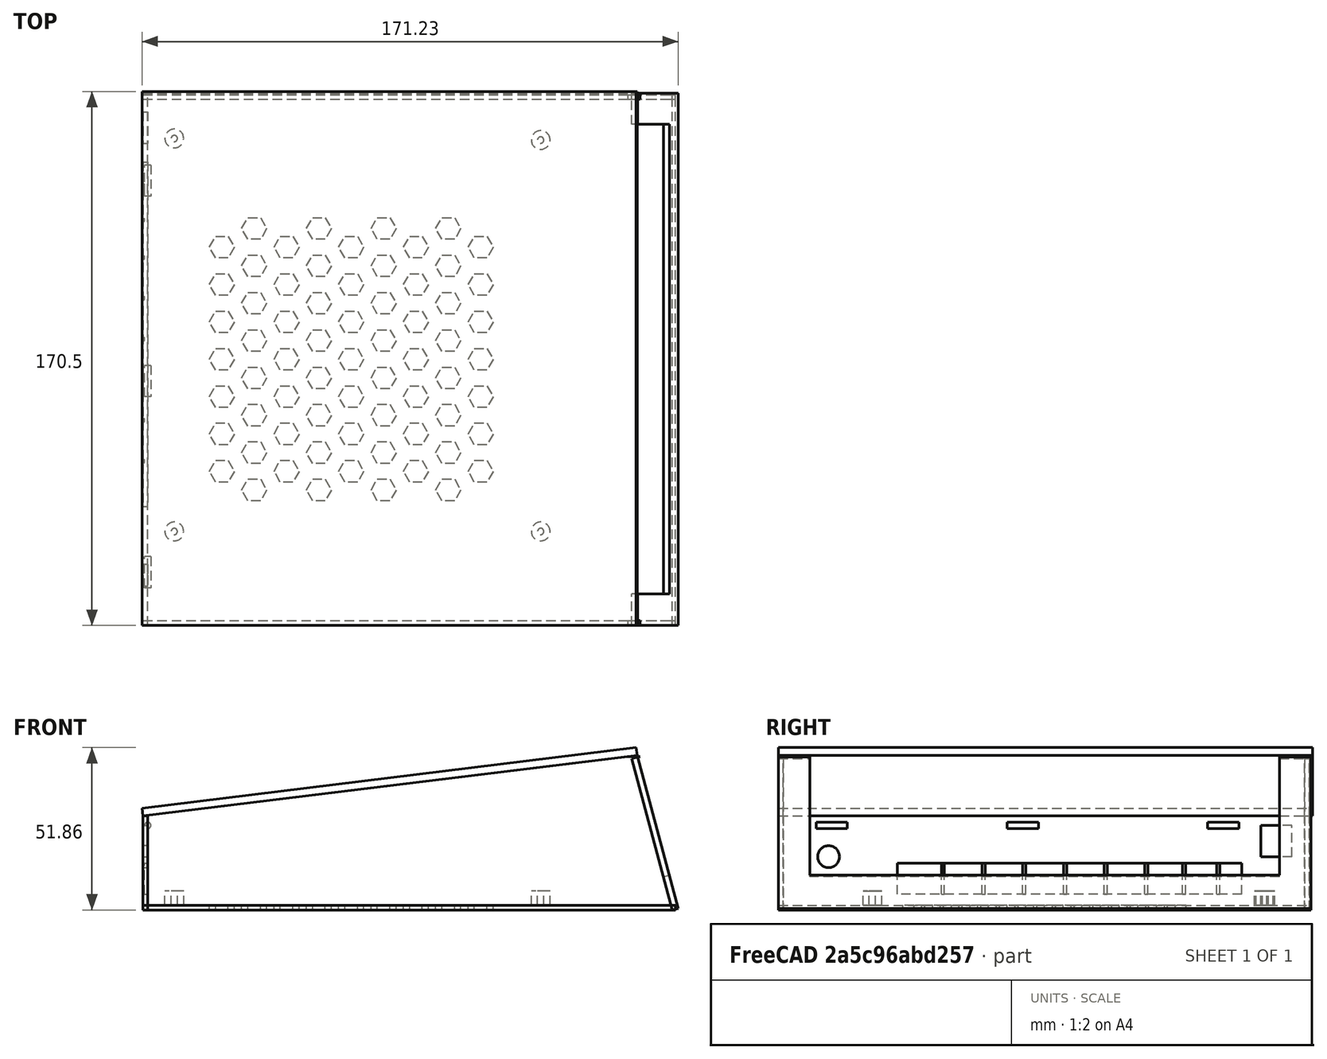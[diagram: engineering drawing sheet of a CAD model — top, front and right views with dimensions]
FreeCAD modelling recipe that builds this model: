
FCSTD DOCUMENT  (FreeCAD 0.20R29603 (Git))
Label: case3
License: All rights reserved
LicenseURL: http://en.wikipedia.org/wiki/All_rights_reserved
objects: Part::Box×21, Part::Cut×9, Part::FeaturePython×5, Part::Cylinder×4, Part::MultiFuse×2, App::DocumentObjectGroup×2
note: 41 computed .brp shape members not serialized (recipe doc carries the construction recipe); baked Part::Feature solids carry a one-line shape summary decoded from their .brp

FEATURE [Part::Box] Box  label="base"
  AttacherType = Attacher::AttachEngine3D
  Height = 1.5
  Length = 170
  Placement = pos=(0,0,-10) rot=(1,0,0;0rad)
  Width = 170
FEATURE [Part::Box] Box001  label="Face"
  AttacherType = Attacher::AttachEngine3D
  Height = 50
  Length = 2
  Placement = pos=(169,0,-10) rot=(0,-1,0;0.261799rad)
  Width = 170
FEATURE [Part::Box] Box002  label="Cube002"
  AttacherType = Attacher::AttachEngine3D
  Height = 30
  Length = 1.5
  Placement = pos=(0,0,-10) rot=(0,0,1;0rad)
  Width = 170
FEATURE [Part::FeaturePython] Tube002  # WARN: FeaturePython — macro-defined, semantics opaque (R4)
  AttacherType = Attacher::AttachEngine3D
  Height = 5
  InnerRadius = 1
  OuterRadius = 3
  Placement = pos=(10,10,-9) rot=(0,0,1;0rad)
FEATURE [Part::FeaturePython] Tube003  # WARN: FeaturePython — macro-defined, semantics opaque (R4)
  AttacherType = Attacher::AttachEngine3D
  Height = 5
  InnerRadius = 1
  OuterRadius = 3
  Placement = pos=(10,135.5,-9) rot=(0,0,1;0rad)
FEATURE [Part::FeaturePython] Tube004  # WARN: FeaturePython — macro-defined, semantics opaque (R4)
  AttacherType = Attacher::AttachEngine3D
  Height = 5
  InnerRadius = 1
  OuterRadius = 3
  Placement = pos=(127,135,-9) rot=(0,0,1;0rad)
FEATURE [Part::FeaturePython] Tube005  # WARN: FeaturePython — macro-defined, semantics opaque (R4)
  AttacherType = Attacher::AttachEngine3D
  Height = 5
  InnerRadius = 1
  OuterRadius = 3
  Placement = pos=(127,10,-9) rot=(0,0,1;0rad)
FEATURE [Part::Box] Box004  label="Cube003"
  AttacherType = Attacher::AttachEngine3D
  Height = 10
  Length = 10
  Placement = pos=(-3,38,-5) rot=(0,0,1;0rad)
  Width = 110
FEATURE [Part::MultiFuse] Fusion003
  Placement = pos=(0,20,0) rot=(0,0,1;0rad)
  Shapes = -> [Tube002,Tube003,Tube004,Tube005]
FEATURE [Part::Cylinder] Cylinder004  label="pwrjack"
  Angle = 360
  AttacherType = Attacher::AttachEngine3D
  FirstAngle = 0
  Height = 10
  Placement = pos=(-3,16,7) rot=(0,1,0;1.5708rad)
  Radius = 3.5
  SecondAngle = 0
FEATURE [Part::Cut] Cut003
  Base = -> Box002
  Tool = -> Cylinder004
FEATURE [Part::Box] Box012  label="Cube010"
  AttacherType = Attacher::AttachEngine3D
  Height = 10
  Length = 0.5
  Placement = pos=(0,65,-5) rot=(0,0,1;0rad)
  Width = 1
FEATURE [Part::Box] Box013  label="Cube011"
  AttacherType = Attacher::AttachEngine3D
  Height = 10
  Length = 0.5
  Placement = pos=(0,52,-5) rot=(0,0,1;0rad)
  Width = 1
FEATURE [Part::Box] Box014  label="Cube012"
  AttacherType = Attacher::AttachEngine3D
  Height = 10
  Length = 0.5
  Placement = pos=(0,78,-5) rot=(0,0,1;0rad)
  Width = 1
FEATURE [Part::Box] Box015  label="Cube013"
  AttacherType = Attacher::AttachEngine3D
  Height = 10
  Length = 0.5
  Placement = pos=(0,91,-5) rot=(0,0,1;0rad)
  Width = 1
FEATURE [Part::Box] Box016  label="Cube014"
  AttacherType = Attacher::AttachEngine3D
  Height = 10
  Length = 0.5
  Placement = pos=(0,104,-5) rot=(0,0,1;0rad)
  Width = 1
FEATURE [Part::Box] Box017  label="Cube015"
  AttacherType = Attacher::AttachEngine3D
  Height = 10
  Length = 0.5
  Placement = pos=(0,117,-5) rot=(0,0,1;0rad)
  Width = 1
FEATURE [Part::Box] Box018  label="Cube016"
  AttacherType = Attacher::AttachEngine3D
  Height = 10
  Length = 0.5
  Placement = pos=(0,129,-5) rot=(0,0,1;0rad)
  Width = 1
FEATURE [Part::Box] Box019  label="Cube017"
  AttacherType = Attacher::AttachEngine3D
  Height = 10
  Length = 0.5
  Placement = pos=(0,140,-5) rot=(0,0,1;0rad)
  Width = 1
FEATURE [Part::MultiFuse] Fusion004
  Shapes = -> [Fusion003,Box]
FEATURE [Part::Cut] Cut
  Base = -> Cut003
  Tool = -> Box004
FEATURE [Part::FeaturePython] HoneycombSolid  # WARN: FeaturePython — macro-defined, semantics opaque (R4)
  Circumradius = 4
  Height = 7
  Length = 81
  Placement = pos=(26,46,-10) rot=(0,0,1;0rad)
  Thickness = 5
  UseContainer = false
  Width = 78
FEATURE [Part::Cut] Cut004
  Base = -> Fusion004
  Tool = -> HoneycombSolid
FEATURE [Part::Box] Box020  label="Face001"
  AttacherType = Attacher::AttachEngine3D
  Height = 40
  Length = 24
  Placement = pos=(164,10,0) rot=(0,-1,0;0.261799rad)
  Width = 150
FEATURE [Part::Cut] Cut005
  Base = -> Box001
  Tool = -> Box020
FEATURE [Part::Box] Box021  label="reset"
  AttacherType = Attacher::AttachEngine3D
  Height = 10
  Length = 10
  Placement = pos=(-2,154,7) rot=(0,0,1;0rad)
  Width = 10
FEATURE [Part::Cut] Cut006
  Base = -> Cut
  Tool = -> Box021
FEATURE [Part::Box] Box005  label="top"
  AttacherType = Attacher::AttachEngine3D
  Height = 2.5
  Length = 159
  Placement = pos=(0,0,20) rot=(0,-1,0;0.122173rad)
  Width = 170.5
FEATURE [App::DocumentObjectGroup] Group001  label="CaseTop"
  Group = -> [Box005]
FEATURE [Part::Box] Box022  label="Cube"
  AttacherType = Attacher::AttachEngine3D
  Height = 49
  Length = 170
  Placement = pos=(0,0,-10) rot=(0,0,1;0rad)
  Width = 1.5
FEATURE [Part::Box] Box023  label="Face002"
  AttacherType = Attacher::AttachEngine3D
  Height = 50
  Length = 25
  Placement = pos=(169,-14,-10) rot=(0,-1,0;0.261799rad)
  Width = 170
FEATURE [Part::Cut] Cut007
  Base = -> Box022
  Tool = -> Box023
FEATURE [Part::Box] Box024  label="top001"
  AttacherType = Attacher::AttachEngine3D
  Height = 20.5
  Length = 159
  Placement = pos=(0,0,20) rot=(0,-1,0;0.122173rad)
  Width = 170.5
FEATURE [Part::Cut] Cut008  label="sidewall"
  Base = -> Cut007
  Tool = -> Box024
FEATURE [Part::Box] Box025  label="Cube018"
  AttacherType = Attacher::AttachEngine3D
  Height = 49
  Length = 170
  Placement = pos=(0,0,-10) rot=(0,0,1;0rad)
  Width = 1.5
FEATURE [Part::Box] Box026  label="Face003"
  AttacherType = Attacher::AttachEngine3D
  Height = 50
  Length = 25
  Placement = pos=(169,-14,-10) rot=(0,-1,0;0.261799rad)
  Width = 170
FEATURE [Part::Box] Box027  label="top002"
  AttacherType = Attacher::AttachEngine3D
  Height = 20.5
  Length = 159
  Placement = pos=(0,0,20) rot=(0,-1,0;0.122173rad)
  Width = 170.5
FEATURE [Part::Cut] Cut009
  Base = -> Box025
  Tool = -> Box026
FEATURE [Part::Cut] Cut010  label="sidewall001"
  Base = -> Cut009
  Placement = pos=(0,168,0) rot=(0,0,1;0rad)
  Tool = -> Box027
FEATURE [Part::Cylinder] Cylinder
  Angle = 360
  AttacherType = Attacher::AttachEngine3D
  FirstAngle = 0
  Height = 10
  Placement = pos=(1.5,22,17) rot=(1,0,0;1.5708rad)
  Radius = 1
  SecondAngle = 0
FEATURE [Part::Cylinder] Cylinder005
  Angle = 360
  AttacherType = Attacher::AttachEngine3D
  FirstAngle = 0
  Height = 10
  Placement = pos=(1.5,83,17) rot=(1,0,0;1.5708rad)
  Radius = 1
  SecondAngle = 0
FEATURE [Part::Cylinder] Cylinder006
  Angle = 360
  AttacherType = Attacher::AttachEngine3D
  FirstAngle = 0
  Height = 10
  Placement = pos=(1.5,147,17) rot=(1,0,0;1.5708rad)
  Radius = 1
  SecondAngle = 0
FEATURE [App::DocumentObjectGroup] Group  label="CaseBase"
  Group = -> [Box012,Box013,Box014,Box015,Box016,Box017,Box018,Box019,Cut004,Cut005,Cut006,Cut010,Cylinder,Cylinder005,Cylinder006,Cut008]
